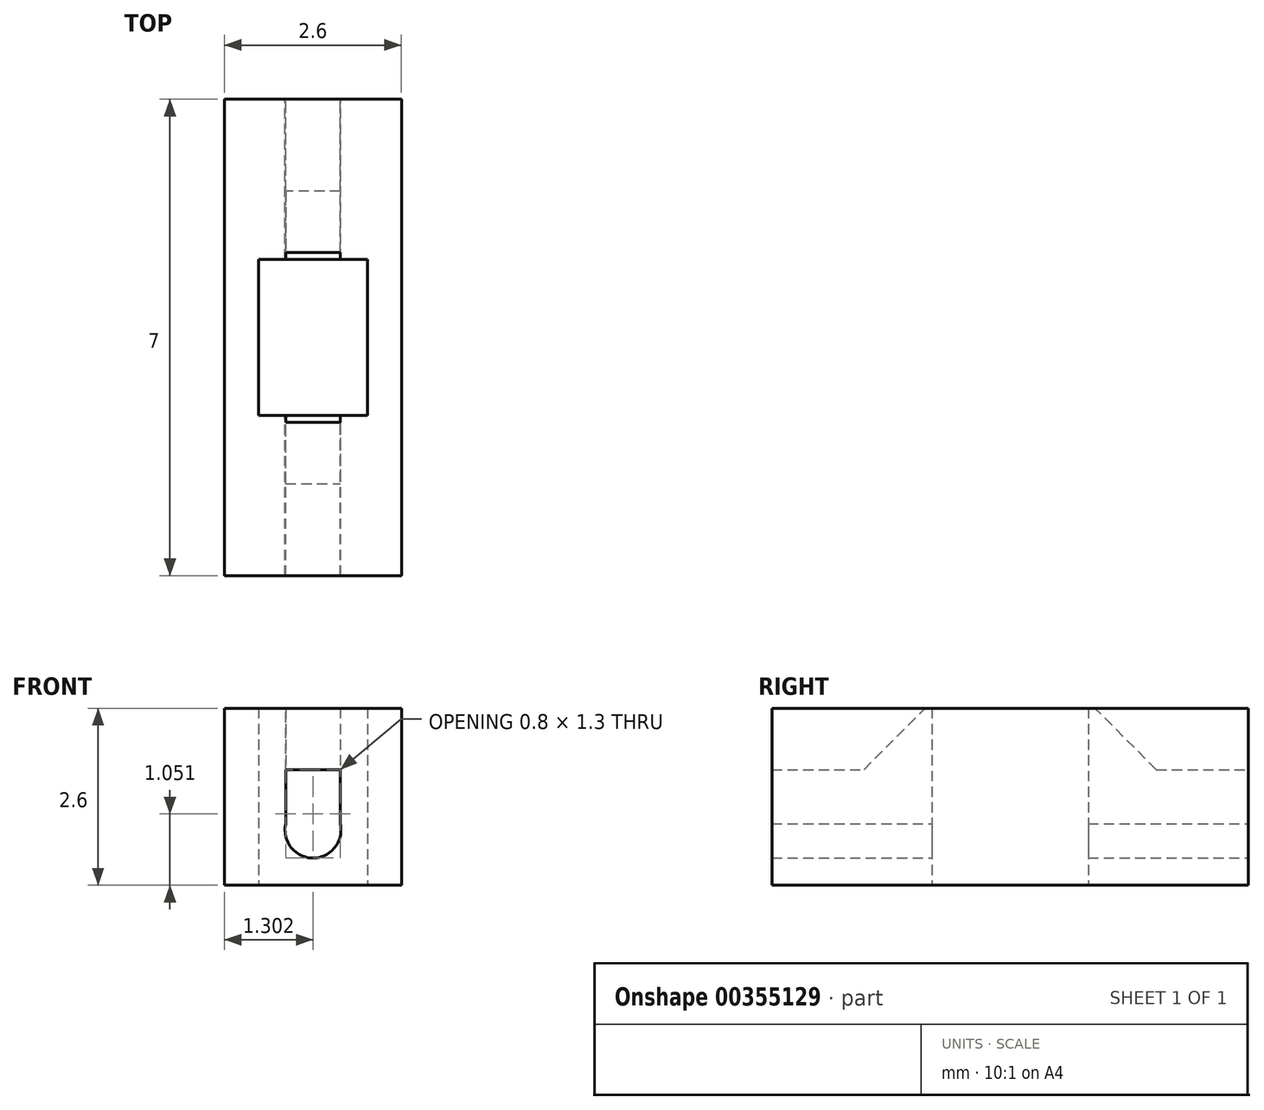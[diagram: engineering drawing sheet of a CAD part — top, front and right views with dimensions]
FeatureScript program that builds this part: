
annotation { "Feature Type Name" : "Feature", "Feature Type Description" : "" }
export const myFeature = defineFeature(function(context is Context, id is Id, definition is map)
    precondition{}
    {
        {
            var Q0;
            Q0=qCreatedBy(makeId("Front.planeOp"),FACE);
            var sketch = newSketch(context, id + "F0", { "sketchPlane" : qUnion([Q0])});
            skLineSegment(sketch, "E0.bottom", {"start": v(1.25, -0.73) * mm, "end": v(3.85, -0.73) * mm});
            skLineSegment(sketch, "E0.top", {"start": v(1.25, -3.33) * mm, "end": v(3.85, -3.33) * mm});
            skLineSegment(sketch, "E0.left", {"start": v(1.25, -0.73) * mm, "end": v(1.25, -3.33) * mm});
            skLineSegment(sketch, "E0.right", {"start": v(3.85, -0.73) * mm, "end": v(3.85, -3.33) * mm});
            skLineSegment(sketch, "E1.bottom", {"start": v(2.15, -1.63) * mm, "end": v(2.95, -1.63) * mm});
            skLineSegment(sketch, "E1.top", {"start": v(2.15, -2.43) * mm, "end": v(2.95, -2.43) * mm});
            skLineSegment(sketch, "E1.left", {"start": v(2.15, -1.63) * mm, "end": v(2.15, -2.43) * mm});
            skLineSegment(sketch, "E1.right", {"start": v(2.95, -1.63) * mm, "end": v(2.95, -2.43) * mm});
            skPoint(sketch, "E1.middle", {"position": v(2.55, -2.03) * mm});
            skPoint(sketch, "E1.middle.positionSnap0", {"position": v(3.85, -2.03) * mm});
            skPoint(sketch, "E1.middle.positionSnap1", {"position": v(2.55, -0.73) * mm});
            skPoint(sketch, "E1.centerSnap0", {"position": v(3.85, -2.03) * mm});
            skPoint(sketch, "E1.centerSnap1", {"position": v(2.55, -0.73) * mm});
            skCircle(sketch, "E2", {"center": v(2.55, -2.52) * mm, "radius": 0.4 * mm});
            skSolve(sketch);
        }
        {
            var Q0;
            Q0=makeQuery(id+"F0.imprint","IMPRINT",FACE,{"disambiguationData":[TD([[makeQuery(id+"F0.imprint","IMPRINT",EDGE,{"derivedFrom":sQuery(id+"F0.wireOp",EDGE,"E0.bottom")}),-1.0]])]});
            extrude(context, id + "F1", {"entities" : qUnion([Q0]), "depth" : 7 * mm});
        }
        {
            var Q0;
            Q0=makeQuery(id+"F1.opExtrude","SWEPT_FACE",FACE,{"disambiguationData":[OSD([sQuery(id+"F0.wireOp",EDGE,"E0.top")])]});
            var sketch = newSketch(context, id + "F2", { "sketchPlane" : qUnion([Q0])});
            skLineSegment(sketch, "E3.bottom", {"start": v(3.35, 4.65) * mm, "end": v(1.75, 4.65) * mm});
            skLineSegment(sketch, "E3.top", {"start": v(3.35, 2.35) * mm, "end": v(1.75, 2.35) * mm});
            skLineSegment(sketch, "E3.left", {"start": v(3.35, 4.65) * mm, "end": v(3.35, 2.35) * mm});
            skLineSegment(sketch, "E3.right", {"start": v(1.75, 4.65) * mm, "end": v(1.75, 2.35) * mm});
            skPoint(sketch, "E3.middle", {"position": v(2.55, 3.5) * mm});
            skPoint(sketch, "E3.middle.positionSnap0", {"position": v(1.25, 3.5) * mm});
            skPoint(sketch, "E3.middle.positionSnap1", {"position": v(2.55, 7) * mm});
            skPoint(sketch, "E3.centerSnap0", {"position": v(1.25, 3.5) * mm});
            skPoint(sketch, "E3.centerSnap1", {"position": v(2.55, 7) * mm});
            skSolve(sketch);
        }
        {
            var Q0;
            Q0=makeQuery(id+"F2.imprint","IMPRINT",FACE,{"disambiguationData":[TD([[makeQuery(id+"F2.imprint","IMPRINT",EDGE,{"derivedFrom":sQuery(id+"F2.wireOp",EDGE,"E3.bottom")}),1.0]])]});
            extrude(context, id + "F3", {"entities" : qUnion([Q0]), "operationType" : NewBodyOperationType.REMOVE, "oppositeDirection" : true, "depth" : 25 * mm});
        }
        {
            var Q0;
            Q0=makeQuery(id+"F3.boolean.opBoolean","INTERSECT",EDGE,{"derivedFrom":[makeQuery(id+"F1.opExtrude","SWEPT_FACE",FACE,{"disambiguationData":[OSD([sQuery(id+"F0.wireOp",EDGE,"E1.bottom")])]}),makeQuery(id+"F3.opExtrude","SWEPT_FACE",FACE,{"disambiguationData":[OSD([sQuery(id+"F2.wireOp",EDGE,"E3.top")])]})]});
            var Q1;
            Q1=makeQuery(id+"F3.boolean.opBoolean","INTERSECT",EDGE,{"derivedFrom":[makeQuery(id+"F1.opExtrude","SWEPT_FACE",FACE,{"disambiguationData":[OSD([sQuery(id+"F0.wireOp",EDGE,"E1.bottom")])]}),makeQuery(id+"F3.opExtrude","SWEPT_FACE",FACE,{"disambiguationData":[OSD([sQuery(id+"F2.wireOp",EDGE,"E3.bottom")])]})]});
            chamfer(context, id + "F4", {"entities" : qUnion([Q0, Q1]), "width" : 1 * mm, "tangentPropagation" : true});
        }
    });
